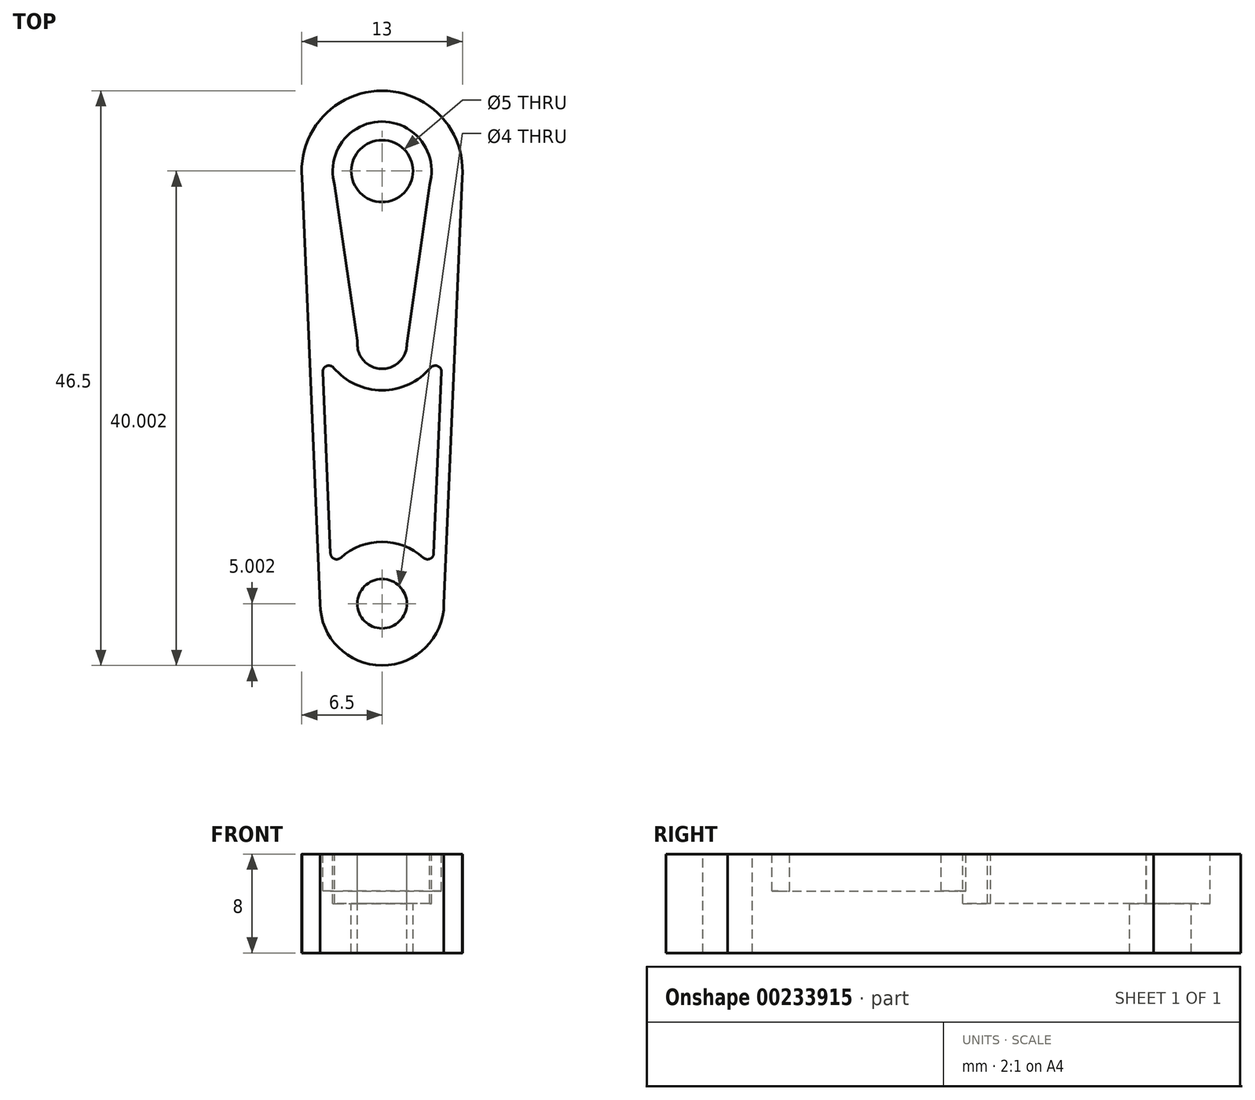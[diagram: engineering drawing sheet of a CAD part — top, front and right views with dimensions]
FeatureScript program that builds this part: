
annotation { "Feature Type Name" : "Feature", "Feature Type Description" : "" }
export const myFeature = defineFeature(function(context is Context, id is Id, definition is map)
    precondition{}
    {
        {
            var Q0;
            Q0=qCreatedBy(makeId("Top.planeOp"),FACE);
            var sketch = newSketch(context, id + "F0", { "sketchPlane" : qUnion([Q0])});
            skCircle(sketch, "E0", {"center": v(0, 49.67) * mm, "radius": 6.5 * mm});
            skCircle(sketch, "E1", {"center": v(0, 14.67) * mm, "radius": 5 * mm});
            skLineSegment(sketch, "E2", {"start": v(6.5, 49.67) * mm, "end": v(5, 14.67) * mm});
            skLineSegment(sketch, "E3", {"start": v(-6.5, 49.67) * mm, "end": v(-5, 14.67) * mm});
            skSolve(sketch);
        }
        {
            var Q0;
            Q0 = qSketchRegion(id + "F0", true);
            extrude(context, id + "F1", {"entities" : qUnion([Q0]), "depth" : 8 * mm});
        }
        {
            var Q0;
            Q0=makeQuery(id+"F1.opExtrude","CAP_FACE",FACE,{"disambiguationData":[OSD([sQuery(id+"F0.wireOp",EDGE,"E0"),sQuery(id+"F0.wireOp",EDGE,"E1"),sQuery(id+"F0.wireOp",EDGE,"E2"),sQuery(id+"F0.wireOp",EDGE,"E3")])],"isStart":false});
            var sketch = newSketch(context, id + "F2", { "sketchPlane" : qUnion([Q0])});
            skCircle(sketch, "E4", {"center": v(0, 49.67) * mm, "radius": 2.5 * mm});
            skCircle(sketch, "E5", {"center": v(0, 14.67) * mm, "radius": 2 * mm});
            skSolve(sketch);
        }
        {
            var Q0;
            Q0 = qSketchRegion(id + "F2", true);
            var Q1;
            Q1 = qSketchRegion(id + "Fm63gqrcfLzPOXp_1", true);
            extrude(context, id + "F3", {"entities" : qUnion([Q0, Q1]), "operationType" : NewBodyOperationType.REMOVE, "oppositeDirection" : true, "depth" : 25 * mm});
        }
        {
            var Q0;
            Q0=makeQuery(id+"F1.opExtrude","CAP_FACE",FACE,{"disambiguationData":[OSD([sQuery(id+"F0.wireOp",EDGE,"E0"),sQuery(id+"F0.wireOp",EDGE,"E1"),sQuery(id+"F0.wireOp",EDGE,"E2"),sQuery(id+"F0.wireOp",EDGE,"E3")])],"isStart":false});
            var sketch = newSketch(context, id + "F4", { "sketchPlane" : qUnion([Q0])});
            skCircle(sketch, "E6", {"center": v(0, 49.67) * mm, "radius": 4 * mm});
            skCircle(sketch, "E7", {"center": v(0, 35.67) * mm, "radius": 2 * mm});
            skLineSegment(sketch, "E8", {"start": v(4, 49.67) * mm, "end": v(2, 35.67) * mm});
            skLineSegment(sketch, "E9", {"start": v(-4, 49.67) * mm, "end": v(-1.98, 35.93) * mm});
            skSolve(sketch);
        }
        {
            var Q0;
            Q0 = qSketchRegion(id + "F4", true);
            extrude(context, id + "F5", {"entities" : qUnion([Q0]), "operationType" : NewBodyOperationType.REMOVE, "oppositeDirection" : true, "depth" : 4 * mm});
        }
        {
            var Q0;
            Q0=makeQuery(id+"F1.opExtrude","CAP_FACE",FACE,{"disambiguationData":[OSD([sQuery(id+"F0.wireOp",EDGE,"E0"),sQuery(id+"F0.wireOp",EDGE,"E1"),sQuery(id+"F0.wireOp",EDGE,"E2"),sQuery(id+"F0.wireOp",EDGE,"E3")])],"isStart":false});
            var sketch = newSketch(context, id + "F6", { "sketchPlane" : qUnion([Q0])});
            skCircle(sketch, "E10", {"center": v(0, 14.67) * mm, "radius": 5 * mm});
            skLineSegment(sketch, "E11", {"start": v(-4.12, 17.5) * mm, "end": v(-4.9, 35.5) * mm});
            skLineSegment(sketch, "E12", {"start": v(4.12, 17.5) * mm, "end": v(4.9, 35.5) * mm});
            skArc(sketch, "E13", {"start": v(-4.9, 35.5) * mm, "mid": v(0, 31.94) * mm, "end": v(4.9, 35.5) * mm});
            skSolve(sketch);
        }
        {
            var Q0;
            {var subQ0=sQuery(id+"F6.wireOp",EDGE,"E11");Q0=makeQuery(id+"F6.imprint","IMPRINT",FACE,{"disambiguationData":[TD([[makeQuery(id+"F6.imprint","IMPRINT",EDGE,{"derivedFrom":subQ0}),-1.0]])]});}
            extrude(context, id + "F7", {"entities" : qUnion([Q0]), "operationType" : NewBodyOperationType.REMOVE, "oppositeDirection" : true, "depth" : 3 * mm});
        }
        {
            var Q0;
            Q0=makeQuery(id+"F7.boolean.opBoolean","COPY",EDGE,{"derivedFrom":makeQuery(id+"F7.opExtrude","SWEPT_EDGE",EDGE,{"disambiguationData":[OSD([sQuery(id+"F6.wireOp",EDGE,"E12"),sQuery(id+"F6.wireOp",EDGE,"E13")])]})});
            fillet(context, id + "F8", {"entities" : qUnion([Q0]), "radius" : 0.5 * mm, "tangentPropagation" : true, "allowEdgeOverflow" : false});
        }
        {
            var Q0;
            Q0=makeQuery(id+"F7.boolean.opBoolean","COPY",EDGE,{"derivedFrom":makeQuery(id+"F7.opExtrude","SWEPT_EDGE",EDGE,{"disambiguationData":[OSD([sQuery(id+"F6.wireOp",EDGE,"E11"),sQuery(id+"F6.wireOp",EDGE,"E13")])]})});
            var Q1;
            Q1=makeQuery(id+"F7.boolean.opBoolean","COPY",EDGE,{"derivedFrom":makeQuery(id+"F7.opExtrude","SWEPT_EDGE",EDGE,{"disambiguationData":[OSD([sQuery(id+"F6.wireOp",EDGE,"E10"),sQuery(id+"F6.wireOp",EDGE,"E12")])]})});
            var Q2;
            Q2=makeQuery(id+"F7.boolean.opBoolean","COPY",EDGE,{"derivedFrom":makeQuery(id+"F7.opExtrude","SWEPT_EDGE",EDGE,{"disambiguationData":[OSD([sQuery(id+"F6.wireOp",EDGE,"E10"),sQuery(id+"F6.wireOp",EDGE,"E11")])]})});
            fillet(context, id + "F9", {"entities" : qUnion([Q0, Q1, Q2]), "radius" : 0.5 * mm, "tangentPropagation" : true, "allowEdgeOverflow" : false});
        }
    });
